# Revit family: Mailboxes_Aluminum-Data_Distribution_System-Salsbury_Industries-4_Unit_High_Wall_Installation
name_source: partatom
category: Specialty Equipment
revit_build: Autodesk Revit 2016 (Build: 20150714_1515(x64)
units: mm (PartAtom-declared; Revit-internal decimal feet)

## family parameters
Always vertical = Yes
Cut with Voids When Loaded = No
Host = Wall
OmniClass Number = 23.40.90.14.11
OmniClass Title = Mail Boxes
Part Type = Normal
Room Calculation Point = No
Round Connector Dimension = Use Diameter
Shared = No

## types (4) — shared parameters
2x4 Platform Support = Softwood, Lumber
Assembly Code = C1030910
Back Enclosure Material = Steel - Salsbury Finish - Clear
Base Depth = 16 "
Front Panel Material = Aluminum - Salsbury Finish - Aluminum
Lock Material = Stainless Steel -Salsbury Finish - Polished
Manufacturer = Salsbury Industries
MasterFormat Number = 10 55 00
MasterFormat Title = Postal Specialties
Model = 2400 Series
OmniClass 23 Number = 23.40.90.14.11
OmniClass 23 Title = Mail Boxes
Platform Material = Plywood
Rack Ladder Height = Rack Ladder Units : 2200C4
Rack Ladder Offset = 0.75 "
Rack Ladder Spacing = 23.875 "
Rough Opening Height = 49.5 "
Trim Material = Steel - Salsbury Finish - Black
Type Comments = Data Distribution System for Aluminum Mailbox Units
URL = www.mailboxes.com
Version = 2.0 (06/30/18)

## per-type parameters (varying)
| type | Description | End Column and Add On Configuration (not applicable) | Left RO Offset | Right RO Offset | Rough Opening Width | Starter Configuration (not applicable) | Starter and Add On Configuration (not applicable) |
| Starter Column-2400 Series Mailboxes-4 High | 4 Unit High  Installation - Starter Column | Yes | 1.5 " | 0 " | 25.375 " | No | No |
| Right Side - Add On Column-2400 Series Mailboxes-4 High | 4 Unit High  Installation - Add On Column | No | 0 " | 0 " | 23.875 " | Yes | No |
| Single Column Installation-2400 Series Mailboxes-4 High | 4 Unit High  Installation - Single Column | Yes | 1.5 " | 1.5 " | 25.375 " | Yes | Yes |
| Right Side - End Column-2400 Series Mailboxes-4 High | 4 Unit High  Installation - End Column | No | 0 " | 1.5 " | 23.875 " | Yes | Yes |

## geometry (parser evidence)
native form markers: Extrusion x1, Sweep x16
no freeform markers — native parametric forms only
